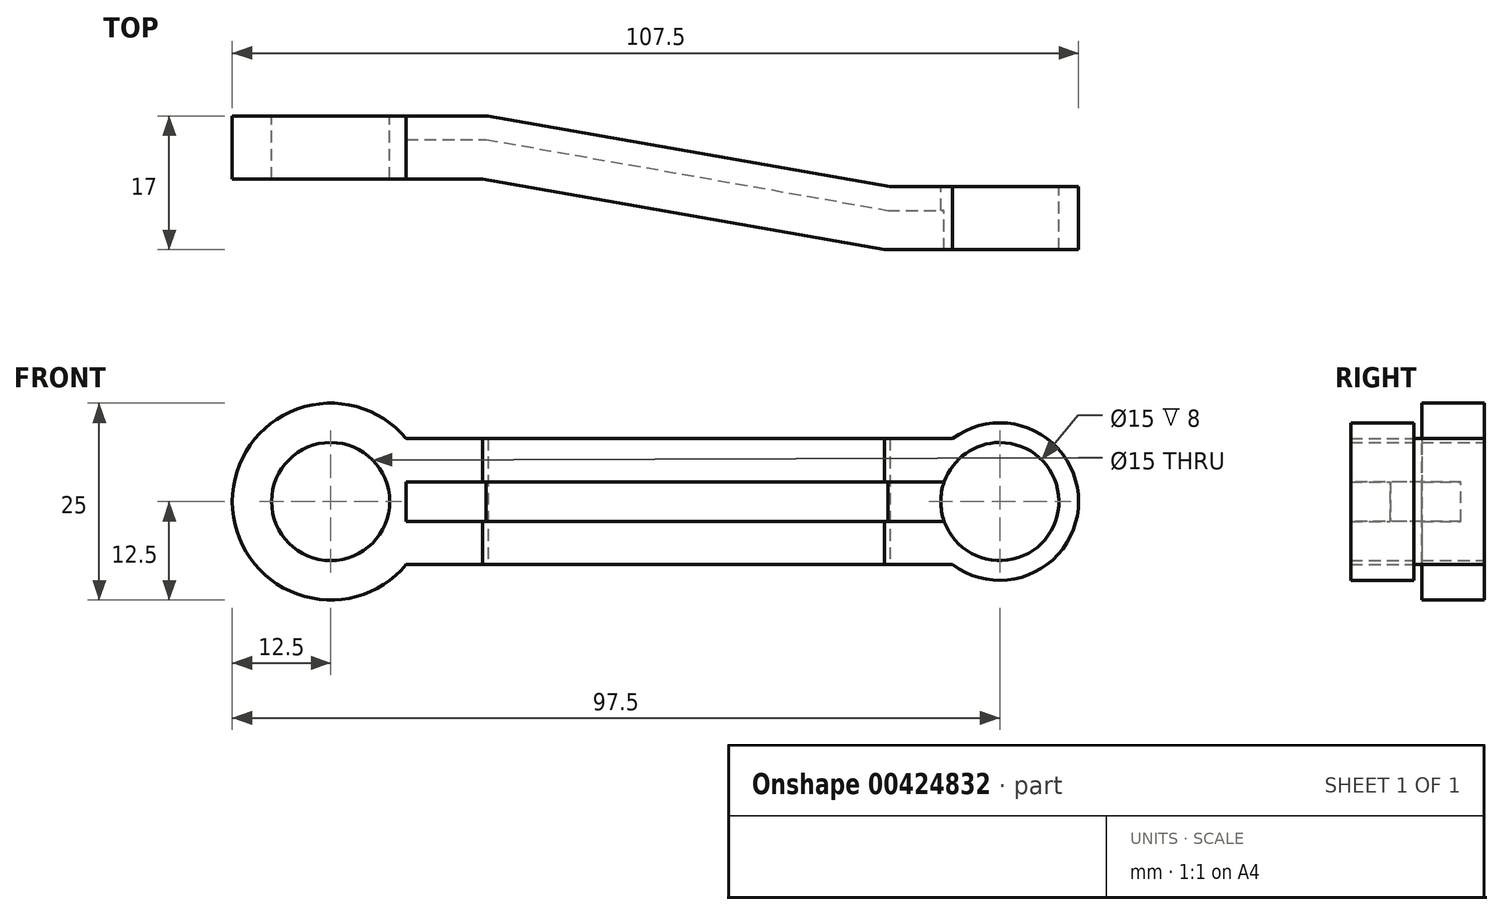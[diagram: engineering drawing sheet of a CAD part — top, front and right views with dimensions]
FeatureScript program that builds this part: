
annotation { "Feature Type Name" : "Feature", "Feature Type Description" : "" }
export const myFeature = defineFeature(function(context is Context, id is Id, definition is map)
    precondition{}
    {
        {
            var Q0;
            Q0=qCreatedBy(makeId("Front.planeOp"),FACE);
            var sketch = newSketch(context, id + "F0", { "sketchPlane" : qUnion([Q0])});
            skCircle(sketch, "E0", {"center": v(0, 0) * mm, "radius": 12.5 * mm});
            skCircle(sketch, "E1", {"center": v(85, 0) * mm, "radius": 10 * mm});
            skLineSegment(sketch, "E2", {"start": v(85, 0) * mm, "end": v(0, 0) * mm, "construction": true});
            skLineSegment(sketch, "E3", {"start": v(9.6, 8) * mm, "end": v(79, 8) * mm});
            skLineSegment(sketch, "E4.MirrorCS", {"start": v(9.6, -8) * mm, "end": v(79, -8) * mm});
            skCircle(sketch, "E5", {"center": v(0, 0) * mm, "radius": 7.5 * mm});
            skCircle(sketch, "E6", {"center": v(85, 0) * mm, "radius": 7.5 * mm});
            skSolve(sketch);
        }
        {
            var Q0;
            Q0=makeQuery(id+"F0.imprint","IMPRINT",FACE,{"disambiguationData":[TD([[makeQuery(id+"F0.imprint","IMPRINT",EDGE,{"derivedFrom":sQuery(id+"F0.wireOp",EDGE,"E5")}),-1.0]])]});
            var Q1;
            Q1=makeQuery(id+"F0.imprint","IMPRINT",FACE,{"disambiguationData":[TD([[makeQuery(id+"F0.imprint","IMPRINT",EDGE,{"derivedFrom":sQuery(id+"F0.wireOp",EDGE,"E6")}),-1.0]])]});
            var Q2;
            {var subQ0=sQuery(id+"F0.wireOp",EDGE,"E3");Q2=makeQuery(id+"F0.imprint","IMPRINT",FACE,{"disambiguationData":[TD([[makeQuery(id+"F0.imprint","IMPRINT",EDGE,{"derivedFrom":subQ0}),-1.0]])]});}
            extrude(context, id + "F1", {"entities" : qUnion([Q0, Q1, Q2]), "depth" : 25 * mm});
        }
        {
            var Q0;
            Q0=qCreatedBy(makeId("Top.planeOp"),FACE);
            var sketch = newSketch(context, id + "F2", { "sketchPlane" : qUnion([Q0])});
            skLineSegment(sketch, "E7", {"start": v(-12.5, 0) * mm, "end": v(20, 0) * mm});
            skLineSegment(sketch, "E8", {"start": v(20, 0) * mm, "end": v(71.04, -9) * mm});
            skLineSegment(sketch, "E9", {"start": v(71.04, -9) * mm, "end": v(95, -9) * mm});
            skLineSegment(sketch, "E10.0", {"start": v(70.34, -17) * mm, "end": v(95, -17) * mm});
            skLineSegment(sketch, "E10.1", {"start": v(19.3, -8) * mm, "end": v(70.34, -17) * mm});
            skLineSegment(sketch, "E10.2", {"start": v(-12.5, -8) * mm, "end": v(19.3, -8) * mm});
            skLineSegment(sketch, "E11", {"start": v(95, -9) * mm, "end": v(95, -17) * mm});
            skLineSegment(sketch, "E12", {"start": v(-12.5, 0) * mm, "end": v(-12.5, -8) * mm});
            skLineSegment(sketch, "E13", {"start": v(95, 0) * mm, "end": v(95, -25) * mm});
            skLineSegment(sketch, "E14", {"start": v(-12.5, -25) * mm, "end": v(-12.5, 0) * mm});
            skSolve(sketch);
        }
        {
            var Q0;
            Q0 = qSketchRegion(id + "F2", true);
            extrude(context, id + "F3", {"entities" : qUnion([Q0]), "operationType" : NewBodyOperationType.INTERSECT, "endBound" : BoundingType.SYMMETRIC, "depth" : 25 * mm});
        }
        {
            var Q0;
            Q0=qCreatedBy(makeId("Top.planeOp"),FACE);
            var sketch = newSketch(context, id + "F4", { "sketchPlane" : qUnion([Q0])});
            skLineSegment(sketch, "E15", {"start": v(9.6, -8) * mm, "end": v(19.3, -8) * mm});
            skLineSegment(sketch, "E16", {"start": v(19.3, -8) * mm, "end": v(70.34, -17) * mm});
            skLineSegment(sketch, "E17", {"start": v(70.34, -17) * mm, "end": v(79, -17) * mm});
            skLineSegment(sketch, "E18.0", {"start": v(70.78, -12) * mm, "end": v(79, -12) * mm});
            skLineSegment(sketch, "E18.1", {"start": v(19.74, -3) * mm, "end": v(70.78, -12) * mm});
            skLineSegment(sketch, "E18.2", {"start": v(9.6, -3) * mm, "end": v(19.74, -3) * mm});
            skLineSegment(sketch, "E19", {"start": v(9.6, -8) * mm, "end": v(9.6, -3) * mm});
            skLineSegment(sketch, "E20", {"start": v(79, -17) * mm, "end": v(79, -12) * mm});
            skLineSegment(sketch, "E21.0", {"start": v(9.6, -3) * mm, "end": v(9.6, -8) * mm});
            skLineSegment(sketch, "E22.0", {"start": v(67.76, -16.54) * mm, "end": v(21.88, -8.46) * mm});
            skPoint(sketch, "E23.orphan", {"position": v(9.6, 0) * mm});
            skPoint(sketch, "E24.orphan", {"position": v(79, -9) * mm});
            skSolve(sketch);
        }
        {
            var Q0;
            Q0 = qSketchRegion(id + "F4", true);
            extrude(context, id + "F5", {"entities" : qUnion([Q0]), "operationType" : NewBodyOperationType.REMOVE, "endBound" : BoundingType.SYMMETRIC, "oppositeDirection" : true, "depth" : 5 * mm});
        }
    });
